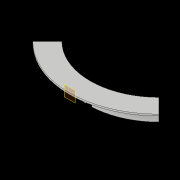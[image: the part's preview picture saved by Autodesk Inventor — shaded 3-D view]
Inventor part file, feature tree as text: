
AUTODESK INVENTOR PART (.ipt)
format: ipt  version: 2017 (Build 210142000, 142)  size: 133,632 bytes
history: native  units: in
note: dims shown in document units (in); Inventor stores cm internally (conversion verified against a paired STEP export)
features: extrude x2, sketch x2, revolve x1, plane x1
ambient origin geometry x8: Origin, YZ Plane, XZ Plane, XY Plane, X Axis, Y Axis, Z Axis, Center Point
bodies: Solid1 (feature_tree)
feature tree (6):
  revolve  "Revolution1"  [1 undecoded]
  plane  "Work Plane1"
  extrude  "Extrusion1"  Depth=0.125in
  extrude  "Extrusion2"  Depth=0.125in
  sketch  "Sketch1"  dims[d0=2.0in d1=5.4375in]
  sketch  "Sketch2"  dims[d2=1.25in d3=0.125in d4=0.125in d5=2.25in d6=1.5in d7=0.125in d8=90.0deg d9=0.5in d10=1.0285in d11=1.0in d12=0.0in d13=1.0285in d14=0.0625in d15=0.25in d16=0.25in d17=135.0deg d18=45.0deg d19=0.0in d20=0.0in]
note: 1 required parameter value undecoded (feature->parameter linkage not recoverable at this tier; creation-order binding heuristic only, values carry confidence <= 0.55)
